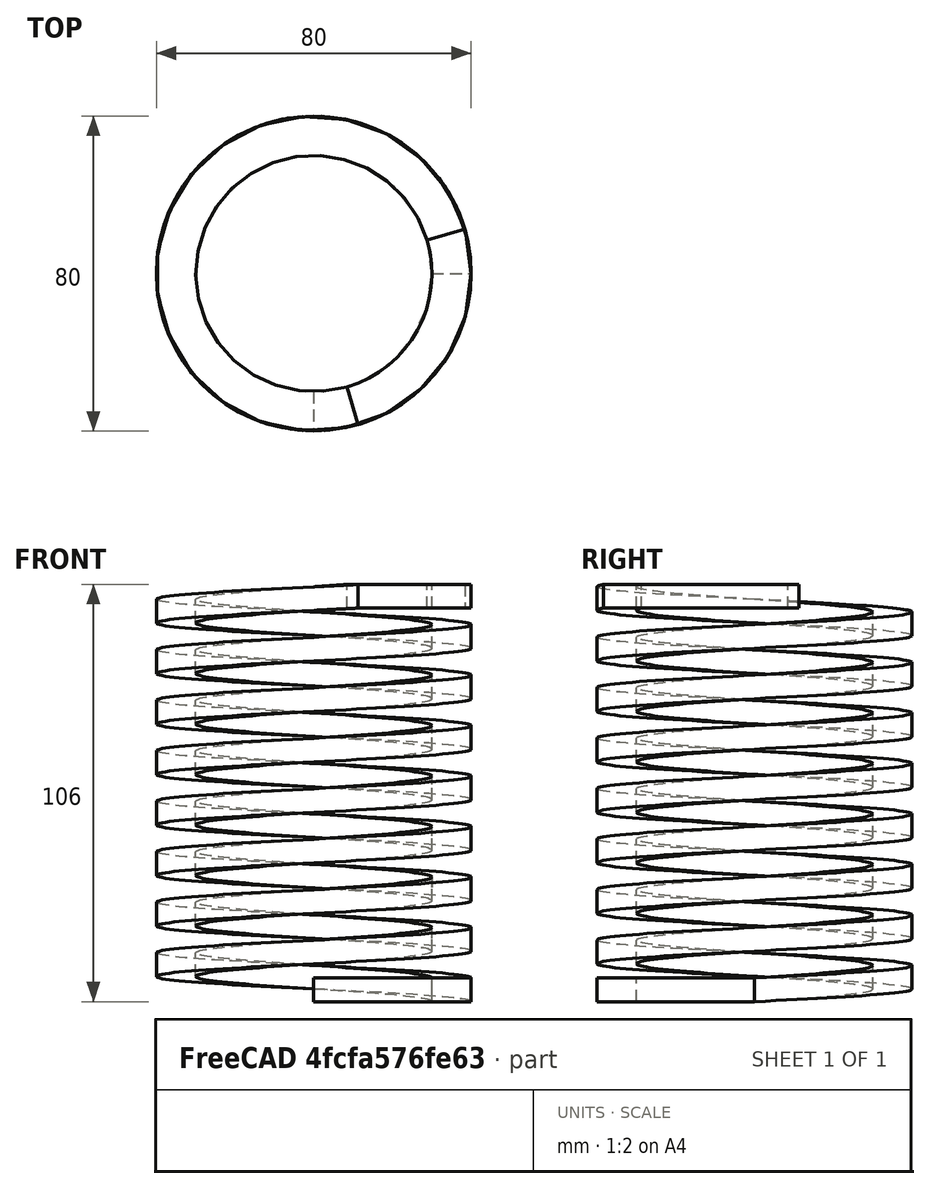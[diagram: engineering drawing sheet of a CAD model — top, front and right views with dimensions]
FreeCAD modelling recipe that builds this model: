
FCSTD DOCUMENT  (FreeCAD 0.19R24276 (Git))
Label: spring
License: All rights reserved
LicenseURL: http://en.wikipedia.org/wiki/All_rights_reserved
objects: PartDesign::Revolution×2, Fem::FemSolverObjectPython×2, Sketcher::SketchObject×1, PartDesign::AdditiveHelix×1, PartDesign::Body×1, App::MaterialObjectPython×1, Fem::ConstraintDisplacement×1, Fem::ConstraintPressure×1, Fem::FemAnalysis×1
note: 8 computed .brp shape members not serialized (recipe doc carries the construction recipe); baked Part::Feature solids carry a one-line shape summary decoded from their .brp

FEATURE [Sketcher::SketchObject] Sketch
  FullyConstrained = true
  MapMode = 5
  Placement = pos=(0,0,0) rot=(1,0,0;1.5708rad)
  Support = -> [XZ_Plane]
  sketch-geometry (4):
    g0: LineSegment StartX=30 StartY=3 StartZ=0 EndX=40 EndY=3 EndZ=0
    g1: LineSegment StartX=40 StartY=3 StartZ=0 EndX=40 EndY=-3 EndZ=0
    g2: LineSegment StartX=40 StartY=-3 StartZ=0 EndX=30 EndY=-3 EndZ=0
    g3: LineSegment StartX=30 StartY=-3 StartZ=0 EndX=30 EndY=3 EndZ=0
  constraints (12):
    c: Coincident(g0,g1)
    c: Coincident(g1,g2)
    c: Coincident(g2,g3)
    c: Coincident(g3,g0)
    c: Horizontal(g0)
    c: Horizontal(g2)
    c: Vertical(g1)
    c: Vertical(g3)
    c: Distance(g0,g-2) = 30
    c: Distance(g1,g2) = 10
    c: Distance(g1) = 6
    c: Distance(g0,g-1) = 3
FEATURE [PartDesign::AdditiveHelix] AdditiveHelix
  Angle = 0
  Axis = (0,2e-16,1)
  Base = (0,0,0)
  HasBeenEdited = true
  Height = 100
  LeftHanded = false
  Mode = 0
  Outside = false
  Pitch = 12.8281
  Placement = pos=(0,0,0) rot=(1,0,0;1.5708rad)
  Profile = -> Sketch
  ReferenceAxis = -> Sketch [V_Axis]
  Turns = 3
FEATURE [PartDesign::Revolution] Revolution
  Angle = 90
  Axis = (-3e-16,3e-16,1)
  Base = (0,0,0)
  BaseFeature = -> AdditiveHelix
  Placement = pos=(0,0,0) rot=(1,0,0;1.5708rad)
  Profile = -> AdditiveHelix [Face1]
  ReferenceAxis = -> Z_Axis
  Reversed = true
FEATURE [PartDesign::Revolution] Revolution001
  Angle = 90
  Axis = (-3e-16,3e-16,1)
  Base = (0,0,0)
  BaseFeature = -> Revolution
  Placement = pos=(0,0,0) rot=(1,0,0;1.5708rad)
  Profile = -> Revolution [Face37]
  ReferenceAxis = -> Z_Axis
FEATURE [PartDesign::Body] Body
  Group = -> [Sketch,AdditiveHelix,Revolution,Revolution001]
  Origin = -> Origin
  Tip = -> Revolution001
FEATURE [Fem::FemSolverObjectPython] SolverCcxTools  # FEM object (typed FeaturePython)
  AnalysisType = 0
  BeamShellResultOutput3D = false
  EigenmodeHighLimit = 1000000
  EigenmodeLowLimit = 0
  EigenmodesCount = 10
  GeometricalNonlinearity = 0
  IterationsControlParameterCutb = 0.25,0.5,0.75,0.85,,,1.5,
  IterationsControlParameterIter = 4,8,9,200,10,400,,200,,
  IterationsControlParameterTimeUse = false
  IterationsThermoMechMaximum = 2000
  IterationsUserDefinedIncrementations = false
  IterationsUserDefinedTimeStepLength = false
  MaterialNonlinearity = 0
  MatrixSolverType = 3
  SplitInputWriter = false
  ThermoMechSteadyState = true
  TimeEnd = 1
  TimeInitialStep = 0.01
FEATURE [App::MaterialObjectPython] MaterialSolid  # material (typed FeaturePython)
  Category = 0
  Material = AuthorAndLicense=Steel-Generic,CardName=Steel-Generic,Density=7900 kg/m^3,+9 more (map truncated)
FEATURE [Fem::ConstraintDisplacement] ConstraintDisplacement
  NormalDirection = (3e-16,-8e-16,-1)
  Normals = (3) [(3.3e-16,-7.82045e-16,-1),(3.3e-16,-7.82045e-16,-1),(3.3e-16,-7.82045e-16,-1)]
  Points = (3) [(40,-2.33613e-15,-3),(26.6667,-26.6667,-3),(-1.43143e-14,-40,-3)]
  References = -> [Revolution001]
  Scale = 5
  rotxFix = false
  rotxFree = true
  rotyFix = false
  rotyFree = true
  rotzFix = false
  rotzFree = true
  xDisplacement = 0
  xFix = true
  xFree = false
  xRotation = 0
  yDisplacement = 0
  yFix = true
  yFree = false
  yRotation = 0
  zDisplacement = 0
  zFix = true
  zFree = false
  zRotation = 0
FEATURE [Fem::ConstraintPressure] ConstraintPressure
  NormalDirection = (-0.281322,0.959614,2.35633e-11)
  Normals = (1) [(-0.281322,0.959614,2.35633e-11)]
  Points = (1) [(33.5865,9.84632,100)]
  Pressure = 1
  References = -> [Revolution001]
FEATURE [Fem::FemSolverObjectPython] SolverFISTRTools  # FEM object (typed FeaturePython)
  AnalysisType = 0
  IncrementType = 0
  InitialTimeIncrement = 1
  MatrixPrecondType = 2
  MatrixSolverIterLog = 0
  MatrixSolverNumIter = 5000
  MatrixSolverResidual = 1e-06
  MatrixSolverTimeLog = 0
  MatrixSolverType = 0
  MaximumTimeIncrement = 1
  MinimumTimeIncrement = 0.0001
  NewtonConvergeResidual = 1e-06
  NewtonMaximumIteration = 20
  Nonlinearity = 1
  OutputFileFormat = 0
  TimeEnd = 1
  n_process = 4
FEATURE [Fem::FemAnalysis] Analysis
  Group = -> [SolverCcxTools,MaterialSolid,ConstraintDisplacement,ConstraintPressure,SolverFISTRTools]
